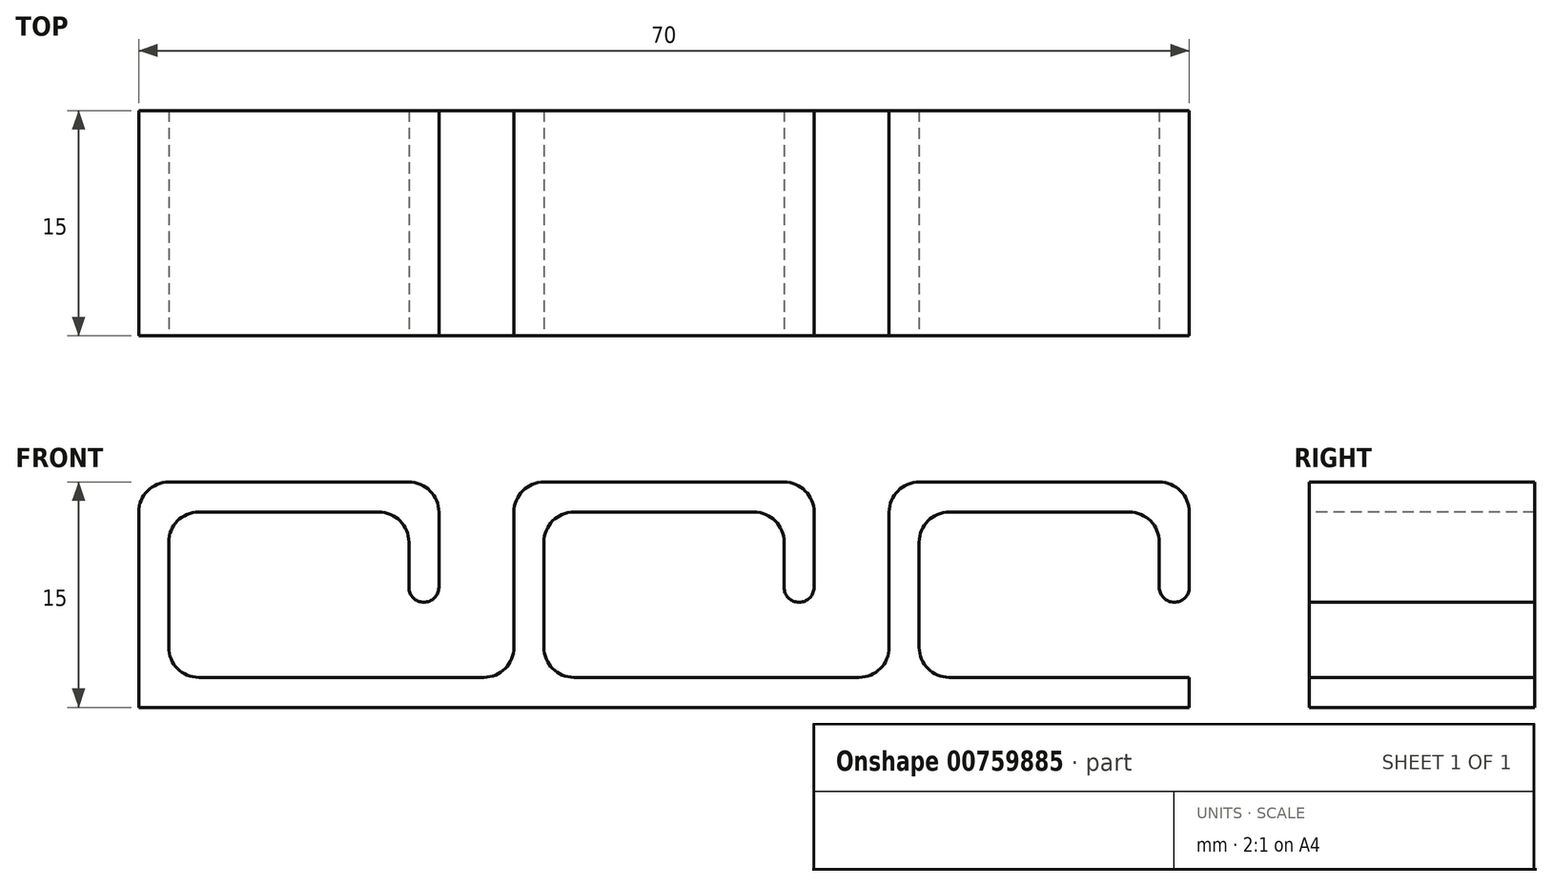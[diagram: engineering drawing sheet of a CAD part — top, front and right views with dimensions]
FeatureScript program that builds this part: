
annotation { "Feature Type Name" : "Feature", "Feature Type Description" : "" }
export const myFeature = defineFeature(function(context is Context, id is Id, definition is map)
    precondition{}
    {
        {
            var Q0;
            Q0=qCreatedBy(makeId("Front.planeOp"),FACE);
            var sketch = newSketch(context, id + "F0", { "sketchPlane" : qUnion([Q0])});
            skPoint(sketch, "E0", {"position": v(0, 0) * mm});
            skLineSegment(sketch, "E1", {"start": v(-12.5, 0) * mm, "end": v(-12.5, 15) * mm});
            skLineSegment(sketch, "E2", {"start": v(-12.5, 15) * mm, "end": v(7.5, 15) * mm});
            skLineSegment(sketch, "E3", {"start": v(7.5, 15) * mm, "end": v(7.5, 7) * mm});
            skLineSegment(sketch, "E4", {"start": v(7.5, 7) * mm, "end": v(5.5, 7) * mm});
            skLineSegment(sketch, "E5", {"start": v(5.5, 7) * mm, "end": v(5.5, 13) * mm});
            skLineSegment(sketch, "E6", {"start": v(5.5, 13) * mm, "end": v(-10.5, 13) * mm});
            skLineSegment(sketch, "E7", {"start": v(-10.5, 13) * mm, "end": v(-10.5, 2) * mm});
            skLineSegment(sketch, "E8", {"start": v(-10.5, 2) * mm, "end": v(12.5, 2) * mm});
            skPoint(sketch, "E9.orphan", {"position": v(12.5, 0) * mm});
            skLineSegment(sketch, "E10.1.0.0", {"start": v(30.5, 13) * mm, "end": v(14.5, 13) * mm});
            skPoint(sketch, "E10.1.0.1", {"position": v(25, 0) * mm});
            skLineSegment(sketch, "E10.1.0.2", {"start": v(14.5, 13) * mm, "end": v(14.5, 2) * mm});
            skPoint(sketch, "E10.1.0.3", {"position": v(37.5, 0) * mm});
            skLineSegment(sketch, "E10.1.0.4", {"start": v(14.5, 2) * mm, "end": v(37.5, 2) * mm});
            skLineSegment(sketch, "E10.1.0.5", {"start": v(32.5, 7) * mm, "end": v(30.5, 7) * mm});
            skLineSegment(sketch, "E10.1.0.6", {"start": v(30.5, 7) * mm, "end": v(30.5, 13) * mm});
            skLineSegment(sketch, "E10.1.0.7", {"start": v(32.5, 15) * mm, "end": v(32.5, 7) * mm});
            skLineSegment(sketch, "E10.1.0.8", {"start": v(12.5, 15) * mm, "end": v(32.5, 15) * mm});
            skLineSegment(sketch, "E10.1.0.9", {"start": v(12.5, 2) * mm, "end": v(12.5, 15) * mm});
            skLineSegment(sketch, "E10.2.0.0", {"start": v(55.5, 13) * mm, "end": v(39.5, 13) * mm});
            skPoint(sketch, "E10.2.0.1", {"position": v(50, 0) * mm});
            skLineSegment(sketch, "E10.2.0.2", {"start": v(39.5, 13) * mm, "end": v(39.5, 2) * mm});
            skLineSegment(sketch, "E10.2.0.4", {"start": v(39.5, 2) * mm, "end": v(57.5, 2) * mm});
            skLineSegment(sketch, "E10.2.0.5", {"start": v(57.5, 7) * mm, "end": v(55.5, 7) * mm});
            skLineSegment(sketch, "E10.2.0.6", {"start": v(55.5, 7) * mm, "end": v(55.5, 13) * mm});
            skLineSegment(sketch, "E10.2.0.7", {"start": v(57.5, 15) * mm, "end": v(57.5, 7) * mm});
            skLineSegment(sketch, "E10.2.0.8", {"start": v(37.5, 15) * mm, "end": v(57.5, 15) * mm});
            skLineSegment(sketch, "E10.2.0.9", {"start": v(37.5, 2) * mm, "end": v(37.5, 15) * mm});
            skLineSegment(sketch, "E10.direction1", {"start": v(-12.5, 0) * mm, "end": v(57.5, 0) * mm});
            skLineSegment(sketch, "E11", {"start": v(57.5, 2) * mm, "end": v(57.5, 0) * mm});
            skSolve(sketch);
        }
        {
            var Q0;
            Q0=makeQuery(id+"F0.imprint","IMPRINT",FACE,{"disambiguationData":[TD([[makeQuery(id+"F0.imprint","IMPRINT",EDGE,{"derivedFrom":sQuery(id+"F0.wireOp",EDGE,"E1")}),-1.0]])]});
            extrude(context, id + "F1", {"entities" : qUnion([Q0]), "oppositeDirection" : true, "depth" : 15 * mm, "offsetDistance" : 25 * mm});
        }
        {
            var Q0;
            Q0=makeQuery(id+"F1.opExtrude","SWEPT_EDGE",EDGE,{"disambiguationData":[OSD([sQuery(id+"F0.wireOp",EDGE,"E7"),sQuery(id+"F0.wireOp",EDGE,"E8")])]});
            var Q1;
            Q1=makeQuery(id+"F1.opExtrude","SWEPT_EDGE",EDGE,{"disambiguationData":[OSD([sQuery(id+"F0.wireOp",EDGE,"E10.1.0.2"),sQuery(id+"F0.wireOp",EDGE,"E10.1.0.4")])]});
            var Q2;
            Q2=makeQuery(id+"F1.opExtrude","SWEPT_EDGE",EDGE,{"disambiguationData":[OSD([sQuery(id+"F0.wireOp",EDGE,"E10.2.0.2"),sQuery(id+"F0.wireOp",EDGE,"E10.2.0.4")])]});
            var Q3;
            Q3=makeQuery(id+"F1.opExtrude","SWEPT_EDGE",EDGE,{"disambiguationData":[OSD([sQuery(id+"F0.wireOp",EDGE,"E6"),sQuery(id+"F0.wireOp",EDGE,"E7")])]});
            var Q4;
            Q4=makeQuery(id+"F1.opExtrude","SWEPT_EDGE",EDGE,{"disambiguationData":[OSD([sQuery(id+"F0.wireOp",EDGE,"E10.1.0.0"),sQuery(id+"F0.wireOp",EDGE,"E10.1.0.2")])]});
            var Q5;
            Q5=makeQuery(id+"F1.opExtrude","SWEPT_EDGE",EDGE,{"disambiguationData":[OSD([sQuery(id+"F0.wireOp",EDGE,"E10.2.0.0"),sQuery(id+"F0.wireOp",EDGE,"E10.2.0.2")])]});
            var Q6;
            Q6=makeQuery(id+"F1.opExtrude","SWEPT_EDGE",EDGE,{"disambiguationData":[OSD([sQuery(id+"F0.wireOp",EDGE,"E10.2.0.8"),sQuery(id+"F0.wireOp",EDGE,"E10.2.0.9")])]});
            var Q7;
            Q7=makeQuery(id+"F1.opExtrude","SWEPT_EDGE",EDGE,{"disambiguationData":[OSD([sQuery(id+"F0.wireOp",EDGE,"E10.1.0.8"),sQuery(id+"F0.wireOp",EDGE,"E10.1.0.9")])]});
            var Q8;
            Q8=makeQuery(id+"F1.opExtrude","SWEPT_EDGE",EDGE,{"disambiguationData":[OSD([sQuery(id+"F0.wireOp",EDGE,"E1"),sQuery(id+"F0.wireOp",EDGE,"E2")])]});
            var Q9;
            Q9=makeQuery(id+"F1.opExtrude","SWEPT_EDGE",EDGE,{"disambiguationData":[OSD([sQuery(id+"F0.wireOp",EDGE,"E2"),sQuery(id+"F0.wireOp",EDGE,"E3")])]});
            var Q10;
            Q10=makeQuery(id+"F1.opExtrude","SWEPT_EDGE",EDGE,{"disambiguationData":[OSD([sQuery(id+"F0.wireOp",EDGE,"E10.1.0.7"),sQuery(id+"F0.wireOp",EDGE,"E10.1.0.8")])]});
            var Q11;
            Q11=makeQuery(id+"F1.opExtrude","SWEPT_EDGE",EDGE,{"disambiguationData":[OSD([sQuery(id+"F0.wireOp",EDGE,"E10.2.0.7"),sQuery(id+"F0.wireOp",EDGE,"E10.2.0.8")])]});
            var Q12;
            Q12=makeQuery(id+"F1.opExtrude","SWEPT_EDGE",EDGE,{"disambiguationData":[OSD([sQuery(id+"F0.wireOp",EDGE,"E5"),sQuery(id+"F0.wireOp",EDGE,"E6")])]});
            var Q13;
            Q13=makeQuery(id+"F1.opExtrude","SWEPT_EDGE",EDGE,{"disambiguationData":[OSD([sQuery(id+"F0.wireOp",EDGE,"E10.1.0.0"),sQuery(id+"F0.wireOp",EDGE,"E10.1.0.6")])]});
            var Q14;
            Q14=makeQuery(id+"F1.opExtrude","SWEPT_EDGE",EDGE,{"disambiguationData":[OSD([sQuery(id+"F0.wireOp",EDGE,"E10.2.0.0"),sQuery(id+"F0.wireOp",EDGE,"E10.2.0.6")])]});
            fillet(context, id + "F2", {"entities" : qUnion([Q0, Q1, Q2, Q3, Q4, Q5, Q6, Q7, Q8, Q9, Q10, Q11, Q12, Q13, Q14]), "radius" : 2 * mm, "tangentPropagation" : true, "allowEdgeOverflow" : false});
        }
        {
            var Q0;
            Q0=makeQuery(id+"F1.opExtrude","SWEPT_EDGE",EDGE,{"disambiguationData":[OSD([sQuery(id+"F0.wireOp",EDGE,"E3"),sQuery(id+"F0.wireOp",EDGE,"E4")])]});
            var Q1;
            Q1=makeQuery(id+"F1.opExtrude","SWEPT_EDGE",EDGE,{"disambiguationData":[OSD([sQuery(id+"F0.wireOp",EDGE,"E4"),sQuery(id+"F0.wireOp",EDGE,"E5")])]});
            var Q2;
            Q2=makeQuery(id+"F1.opExtrude","SWEPT_EDGE",EDGE,{"disambiguationData":[OSD([sQuery(id+"F0.wireOp",EDGE,"E10.1.0.5"),sQuery(id+"F0.wireOp",EDGE,"E10.1.0.7")])]});
            var Q3;
            Q3=makeQuery(id+"F1.opExtrude","SWEPT_EDGE",EDGE,{"disambiguationData":[OSD([sQuery(id+"F0.wireOp",EDGE,"E10.1.0.5"),sQuery(id+"F0.wireOp",EDGE,"E10.1.0.6")])]});
            var Q4;
            Q4=makeQuery(id+"F1.opExtrude","SWEPT_EDGE",EDGE,{"disambiguationData":[OSD([sQuery(id+"F0.wireOp",EDGE,"E10.2.0.5"),sQuery(id+"F0.wireOp",EDGE,"E10.2.0.7")])]});
            var Q5;
            Q5=makeQuery(id+"F1.opExtrude","SWEPT_EDGE",EDGE,{"disambiguationData":[OSD([sQuery(id+"F0.wireOp",EDGE,"E10.2.0.5"),sQuery(id+"F0.wireOp",EDGE,"E10.2.0.6")])]});
            fillet(context, id + "F3", {"entities" : qUnion([Q0, Q1, Q2, Q3, Q4, Q5]), "radius" : 1 * mm, "tangentPropagation" : true, "allowEdgeOverflow" : false});
        }
        {
            var Q0;
            Q0=makeQuery(id+"F1.opExtrude","SWEPT_EDGE",EDGE,{"disambiguationData":[OSD([sQuery(id+"F0.wireOp",EDGE,"E8"),sQuery(id+"F0.wireOp",EDGE,"E10.1.0.9")])]});
            var Q1;
            Q1=makeQuery(id+"F1.opExtrude","SWEPT_EDGE",EDGE,{"disambiguationData":[OSD([sQuery(id+"F0.wireOp",EDGE,"E10.1.0.4"),sQuery(id+"F0.wireOp",EDGE,"E10.2.0.9")])]});
            fillet(context, id + "F4", {"entities" : qUnion([Q0, Q1]), "radius" : 2 * mm, "tangentPropagation" : true, "allowEdgeOverflow" : false});
        }
    });
